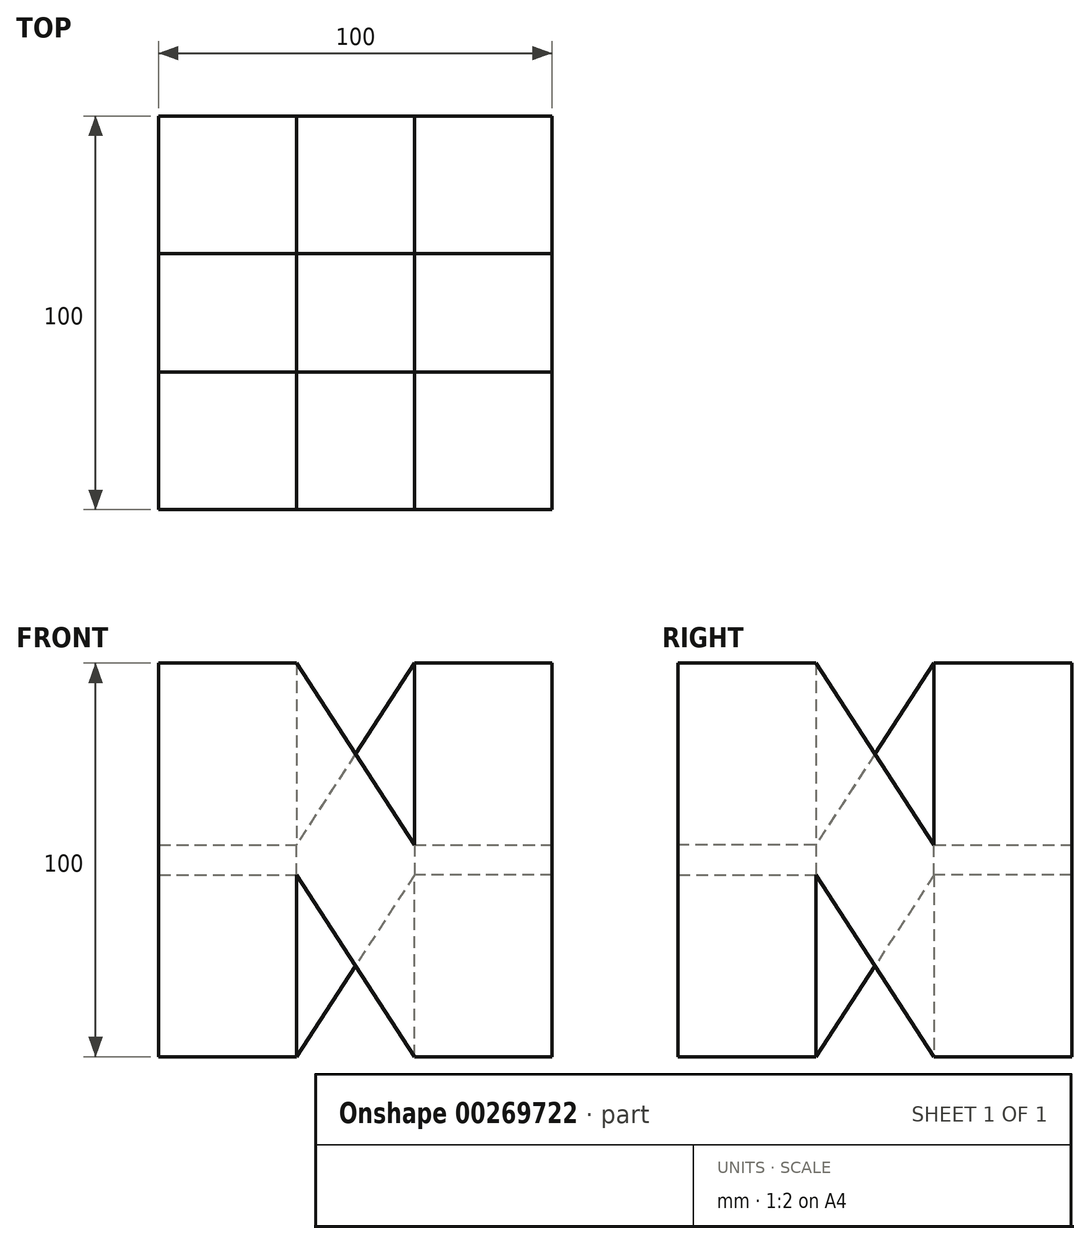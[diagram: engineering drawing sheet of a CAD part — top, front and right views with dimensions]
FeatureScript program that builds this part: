
annotation { "Feature Type Name" : "Feature", "Feature Type Description" : "" }
export const myFeature = defineFeature(function(context is Context, id is Id, definition is map)
    precondition{}
    {
        {
            var Q0;
            Q0=qCreatedBy(makeId("Top.planeOp"),FACE);
            var sketch = newSketch(context, id + "F0", { "sketchPlane" : qUnion([Q0])});
            skLineSegment(sketch, "E0.bottom", {"start": v(50, 50) * mm, "end": v(-50, 50) * mm});
            skLineSegment(sketch, "E0.top", {"start": v(50, -50) * mm, "end": v(-50, -50) * mm});
            skLineSegment(sketch, "E0.left", {"start": v(50, 50) * mm, "end": v(50, -50) * mm});
            skLineSegment(sketch, "E0.right", {"start": v(-50, 50) * mm, "end": v(-50, -50) * mm});
            skPoint(sketch, "E0.middle", {"position": v(0, 0) * mm});
            skLineSegment(sketch, "E1.bottom", {"start": v(50, 50) * mm, "end": v(15, 50) * mm});
            skLineSegment(sketch, "E1.top", {"start": v(50, 15) * mm, "end": v(15, 15) * mm});
            skLineSegment(sketch, "E1.left", {"start": v(50, 50) * mm, "end": v(50, 15) * mm});
            skLineSegment(sketch, "E1.right", {"start": v(15, 50) * mm, "end": v(15, 15) * mm});
            skLineSegment(sketch, "E2.bottom", {"start": v(50, -50) * mm, "end": v(15, -50) * mm});
            skLineSegment(sketch, "E2.top", {"start": v(50, -15) * mm, "end": v(15, -15) * mm});
            skLineSegment(sketch, "E2.left", {"start": v(50, -50) * mm, "end": v(50, -15) * mm});
            skLineSegment(sketch, "E2.right", {"start": v(15, -50) * mm, "end": v(15, -15) * mm});
            skLineSegment(sketch, "E3.bottom", {"start": v(-50, -50) * mm, "end": v(-15, -50) * mm});
            skLineSegment(sketch, "E3.top", {"start": v(-50, -15) * mm, "end": v(-15, -15) * mm});
            skLineSegment(sketch, "E3.left", {"start": v(-50, -50) * mm, "end": v(-50, -15) * mm});
            skLineSegment(sketch, "E3.right", {"start": v(-15, -50) * mm, "end": v(-15, -15) * mm});
            skLineSegment(sketch, "E4.bottom", {"start": v(-50, 50) * mm, "end": v(-15, 50) * mm});
            skLineSegment(sketch, "E4.top", {"start": v(-50, 15) * mm, "end": v(-15, 15) * mm});
            skLineSegment(sketch, "E4.left", {"start": v(-50, 50) * mm, "end": v(-50, 15) * mm});
            skLineSegment(sketch, "E4.right", {"start": v(-15, 50) * mm, "end": v(-15, 15) * mm});
            skSolve(sketch);
        }
        {
            var Q0;
            Q0=qCreatedBy(makeId("Top.planeOp"),FACE);
            cPlane(context, id + "F1", {"entities" : qUnion([Q0]), "cplaneType" : CPlaneType.OFFSET, "offset" : 100 * mm, "width" : 150 * mm, "height" : 150 * mm});
        }
        {
            var Q0;
            Q0=qCreatedBy(id+"F1.planeOp",FACE);
            var sketch = newSketch(context, id + "F2", { "sketchPlane" : qUnion([Q0])});
            skLineSegment(sketch, "E5.0.0", {"start": v(-15, 15) * mm, "end": v(-15, 50) * mm});
            skLineSegment(sketch, "E5.0.1", {"start": v(-15, 50) * mm, "end": v(-50, 50) * mm});
            skLineSegment(sketch, "E5.0.2", {"start": v(-50, 50) * mm, "end": v(-50, 15) * mm});
            skLineSegment(sketch, "E5.0.3", {"start": v(-50, 15) * mm, "end": v(-15, 15) * mm});
            skLineSegment(sketch, "E6.0.0", {"start": v(50, 50) * mm, "end": v(15, 50) * mm});
            skLineSegment(sketch, "E6.0.1", {"start": v(15, 50) * mm, "end": v(15, 15) * mm});
            skLineSegment(sketch, "E6.0.2", {"start": v(15, 15) * mm, "end": v(50, 15) * mm});
            skLineSegment(sketch, "E6.0.3", {"start": v(50, 15) * mm, "end": v(50, 50) * mm});
            skLineSegment(sketch, "E7.0.0", {"start": v(15, -50) * mm, "end": v(50, -50) * mm});
            skLineSegment(sketch, "E7.0.1", {"start": v(50, -50) * mm, "end": v(50, -15) * mm});
            skLineSegment(sketch, "E7.0.2", {"start": v(50, -15) * mm, "end": v(15, -15) * mm});
            skLineSegment(sketch, "E7.0.3", {"start": v(15, -15) * mm, "end": v(15, -50) * mm});
            skLineSegment(sketch, "E8.0.0", {"start": v(-50, -15) * mm, "end": v(-50, -50) * mm});
            skLineSegment(sketch, "E8.0.1", {"start": v(-50, -50) * mm, "end": v(-15, -50) * mm});
            skLineSegment(sketch, "E8.0.2", {"start": v(-15, -50) * mm, "end": v(-15, -15) * mm});
            skLineSegment(sketch, "E8.0.3", {"start": v(-15, -15) * mm, "end": v(-50, -15) * mm});
            skSolve(sketch);
        }
        {
            var Q0;
            Q0=makeQuery(id+"F2.imprint","IMPRINT",FACE,{"disambiguationData":[TD([[makeQuery(id+"F2.imprint","IMPRINT",EDGE,{"derivedFrom":sQuery(id+"F2.wireOp",EDGE,"E8.0.0")}),1.0]])]});
            var Q1;
            {var subQ4=sQuery(id+"F0.wireOp",EDGE,"E3.top");Q1=makeQuery(id+"F0.imprint","IMPRINT",FACE,{"disambiguationData":[TD([[makeQuery(id+"F0.imprint","IMPRINT",EDGE,{"derivedFrom":subQ4}),-1.0]])]});}
            loft(context, id + "F3", {"sheetProfilesArray" : [{ "sheetProfileEntities" : qUnion([Q0]) }, { "sheetProfileEntities" : qUnion([Q1]) }]});
        }
        {
            var Q1;
            {var subQ4=sQuery(id+"F0.wireOp",EDGE,"E2.top");Q1=makeQuery(id+"F0.imprint","IMPRINT",FACE,{"disambiguationData":[TD([[makeQuery(id+"F0.imprint","IMPRINT",EDGE,{"derivedFrom":subQ4}),1.0]])]});}
            var Q2;
            Q2=makeQuery(id+"F2.imprint","IMPRINT",FACE,{"disambiguationData":[TD([[makeQuery(id+"F2.imprint","IMPRINT",EDGE,{"derivedFrom":sQuery(id+"F2.wireOp",EDGE,"E8.0.0")}),1.0]])]});
            loft(context, id + "F4", {"operationType" : NewBodyOperationType.ADD, "sheetProfilesArray" : [{ "sheetProfileEntities" : qUnion([Q1]) }, { "sheetProfileEntities" : qUnion([Q2]) }]});
        }
        {
            var Q1;
            {var subQ4=sQuery(id+"F0.wireOp",EDGE,"E2.top");Q1=makeQuery(id+"F0.imprint","IMPRINT",FACE,{"disambiguationData":[TD([[makeQuery(id+"F0.imprint","IMPRINT",EDGE,{"derivedFrom":subQ4}),1.0]])]});}
            var Q2;
            Q2=makeQuery(id+"F2.imprint","IMPRINT",FACE,{"disambiguationData":[TD([[makeQuery(id+"F2.imprint","IMPRINT",EDGE,{"derivedFrom":sQuery(id+"F2.wireOp",EDGE,"E7.0.0")}),1.0]])]});
            loft(context, id + "F5", {"operationType" : NewBodyOperationType.ADD, "sheetProfilesArray" : [{ "sheetProfileEntities" : qUnion([Q1]) }, { "sheetProfileEntities" : qUnion([Q2]) }]});
        }
        {
            var Q0;
            {var subQ4=sQuery(id+"F0.wireOp",EDGE,"E1.top");Q0=makeQuery(id+"F0.imprint","IMPRINT",FACE,{"disambiguationData":[TD([[makeQuery(id+"F0.imprint","IMPRINT",EDGE,{"derivedFrom":subQ4}),-1.0]])]});}
            var Q1;
            Q1=makeQuery(id+"F2.imprint","IMPRINT",FACE,{"disambiguationData":[TD([[makeQuery(id+"F2.imprint","IMPRINT",EDGE,{"derivedFrom":sQuery(id+"F2.wireOp",EDGE,"E6.0.0")}),1.0]])]});
            loft(context, id + "F6", {"sheetProfilesArray" : [{ "sheetProfileEntities" : qUnion([Q0]) }, { "sheetProfileEntities" : qUnion([Q1]) }]});
        }
        {
            var Q2;
            {var subQ4=sQuery(id+"F0.wireOp",EDGE,"E1.top");Q2=makeQuery(id+"F0.imprint","IMPRINT",FACE,{"disambiguationData":[TD([[makeQuery(id+"F0.imprint","IMPRINT",EDGE,{"derivedFrom":subQ4}),-1.0]])]});}
            var Q3;
            Q3=makeQuery(id+"F2.imprint","IMPRINT",FACE,{"disambiguationData":[TD([[makeQuery(id+"F2.imprint","IMPRINT",EDGE,{"derivedFrom":sQuery(id+"F2.wireOp",EDGE,"E7.0.0")}),1.0]])]});
            loft(context, id + "F7", {"operationType" : NewBodyOperationType.ADD, "sheetProfilesArray" : [{ "sheetProfileEntities" : qUnion([Q2]) }, { "sheetProfileEntities" : qUnion([Q3]) }]});
        }
        {
            var Q1;
            Q1=makeQuery(id+"F2.imprint","IMPRINT",FACE,{"disambiguationData":[TD([[makeQuery(id+"F2.imprint","IMPRINT",EDGE,{"derivedFrom":sQuery(id+"F2.wireOp",EDGE,"E6.0.0")}),1.0]])]});
            var Q2;
            {var subQ4=sQuery(id+"F0.wireOp",EDGE,"E4.top");Q2=makeQuery(id+"F0.imprint","IMPRINT",FACE,{"disambiguationData":[TD([[makeQuery(id+"F0.imprint","IMPRINT",EDGE,{"derivedFrom":subQ4}),1.0]])]});}
            loft(context, id + "F8", {"operationType" : NewBodyOperationType.ADD, "sheetProfilesArray" : [{ "sheetProfileEntities" : qUnion([Q1]) }, { "sheetProfileEntities" : qUnion([Q2]) }]});
        }
        {
            var Q1;
            Q1=makeQuery(id+"F2.imprint","IMPRINT",FACE,{"disambiguationData":[TD([[makeQuery(id+"F2.imprint","IMPRINT",EDGE,{"derivedFrom":sQuery(id+"F2.wireOp",EDGE,"E5.0.0")}),1.0]])]});
            var Q2;
            {var subQ4=sQuery(id+"F0.wireOp",EDGE,"E4.top");Q2=makeQuery(id+"F0.imprint","IMPRINT",FACE,{"disambiguationData":[TD([[makeQuery(id+"F0.imprint","IMPRINT",EDGE,{"derivedFrom":subQ4}),1.0]])]});}
            loft(context, id + "F9", {"operationType" : NewBodyOperationType.ADD, "sheetProfilesArray" : [{ "sheetProfileEntities" : qUnion([Q1]) }, { "sheetProfileEntities" : qUnion([Q2]) }]});
        }
        {
            var Q1;
            Q1=makeQuery(id+"F2.imprint","IMPRINT",FACE,{"disambiguationData":[TD([[makeQuery(id+"F2.imprint","IMPRINT",EDGE,{"derivedFrom":sQuery(id+"F2.wireOp",EDGE,"E5.0.0")}),1.0]])]});
            var Q2;
            {var subQ4=sQuery(id+"F0.wireOp",EDGE,"E3.top");Q2=makeQuery(id+"F0.imprint","IMPRINT",FACE,{"disambiguationData":[TD([[makeQuery(id+"F0.imprint","IMPRINT",EDGE,{"derivedFrom":subQ4}),-1.0]])]});}
            loft(context, id + "F10", {"operationType" : NewBodyOperationType.ADD, "sheetProfilesArray" : [{ "sheetProfileEntities" : qUnion([Q1]) }, { "sheetProfileEntities" : qUnion([Q2]) }]});
        }
    });
